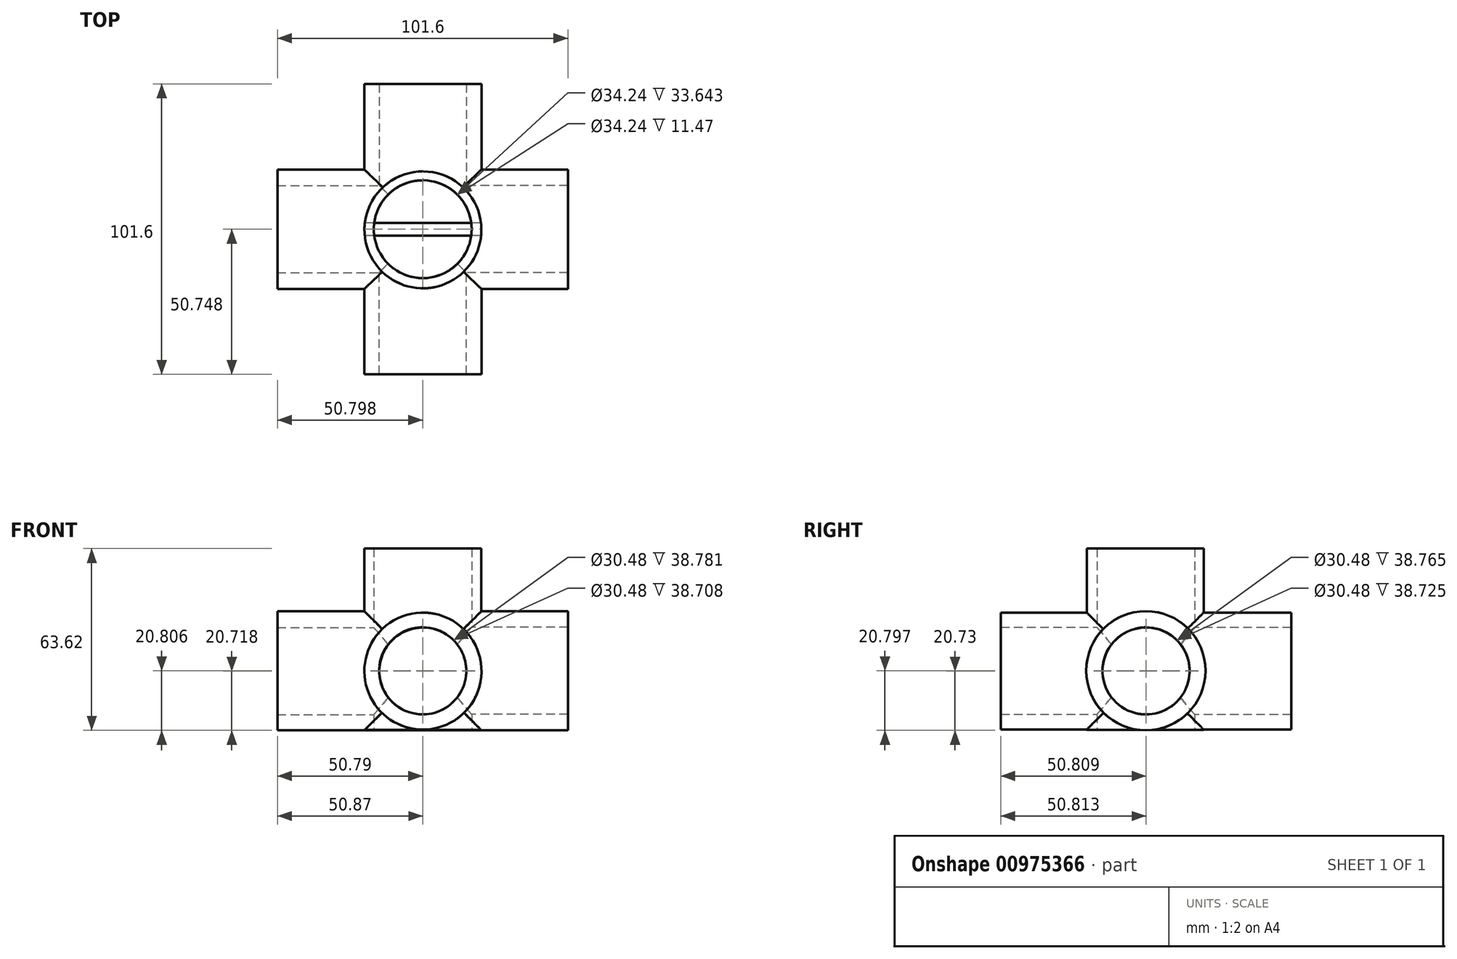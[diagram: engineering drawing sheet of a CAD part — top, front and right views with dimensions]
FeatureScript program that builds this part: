
annotation { "Feature Type Name" : "Feature", "Feature Type Description" : "" }
export const myFeature = defineFeature(function(context is Context, id is Id, definition is map)
    precondition{}
    {
        {
            var Q0;
            Q0=qCreatedBy(makeId("Front.planeOp"),FACE);
            var sketch = newSketch(context, id + "F0", { "sketchPlane" : qUnion([Q0])});
            skCircle(sketch, "E0", {"center": v(0.07, 20.6) * mm, "radius": 20.47 * mm});
            skSolve(sketch);
        }
        {
            var Q0;
            Q0 = qSketchRegion(id + "F0", true);
            extrude(context, id + "F1", {"entities" : qUnion([Q0]), "depth" : 50.8 * mm, "offsetDistance" : 25.4 * mm, "hasSecondDirection" : true, "secondDirectionOppositeDirection" : true, "secondDirectionDepth" : 50.8 * mm});
        }
        {
            var Q0;
            Q0=qCreatedBy(makeId("Top.planeOp"),FACE);
            var sketch = newSketch(context, id + "F2", { "sketchPlane" : qUnion([Q0])});
            skCircle(sketch, "E1", {"center": v(0.07, -0.28) * mm, "radius": 20.46 * mm});
            skSolve(sketch);
        }
        {
            var Q0;
            Q0 = qSketchRegion(id + "F2", true);
            extrude(context, id + "F3", {"entities" : qUnion([Q0]), "operationType" : NewBodyOperationType.ADD, "depth" : 63.5 * mm, "offsetDistance" : 25.4 * mm});
        }
        {
            var Q0;
            Q0=qCreatedBy(makeId("Right.planeOp"),FACE);
            var sketch = newSketch(context, id + "F4", { "sketchPlane" : qUnion([Q0])});
            skCircle(sketch, "E2", {"center": v(-0.07, 20.74) * mm, "radius": 20.86 * mm});
            skSolve(sketch);
        }
        {
            var Q0;
            Q0 = qSketchRegion(id + "F4", true);
            extrude(context, id + "F5", {"entities" : qUnion([Q0]), "operationType" : NewBodyOperationType.ADD, "depth" : 50.8 * mm, "offsetDistance" : 25.4 * mm, "hasSecondDirection" : true, "secondDirectionOppositeDirection" : true, "secondDirectionDepth" : 50.8 * mm});
        }
        {
            var Q0;
            Q0=qCreatedBy(makeId("Right.planeOp"),FACE);
            var sketch = newSketch(context, id + "F6", { "sketchPlane" : qUnion([Q0])});
            skPoint(sketch, "E3", {"position": v(0, 20.61) * mm});
            skSolve(sketch);
        }
        {
            var Q0;
            Q0=sQuery(id+"F6.wireOp",VERTEX,"E3");
            var Q1;
            Q1=makeQuery(id+"F1.opExtrude","SWEPT_BODY",BODY,{"disambiguationData":[OSD([sQuery(id+"F0.wireOp",EDGE,"E0")])]});
            hole(context, id + "F7", {"style" : HoleStyle.SIMPLE, "endStyle" : HoleEndStyle.THROUGH, "holeDiameter" : 30.48 * mm, "majorDiameter" : 6.35 * mm, "isTappedThrough" : true, "tappedDepth" : 12.7 * mm, "tapClearance" : 3, "locations" : qUnion([Q0]), "scope" : qUnion([Q1])});
        }
        {
            var Q0;
            Q0=qCreatedBy(makeId("Right.planeOp"),FACE);
            var sketch = newSketch(context, id + "F8", { "sketchPlane" : qUnion([Q0])});
            skPoint(sketch, "E4", {"position": v(0.01, 20.68) * mm});
            skSolve(sketch);
        }
        {
            var Q0;
            Q0=sQuery(id+"F0.wireOp",VERTEX,"E0.center");
            var Q1;
            Q1=makeQuery(id+"F1.opExtrude","SWEPT_BODY",BODY,{"disambiguationData":[OSD([sQuery(id+"F0.wireOp",EDGE,"E0")])]});
            hole(context, id + "F9", {"style" : HoleStyle.SIMPLE, "endStyle" : HoleEndStyle.THROUGH, "holeDiameter" : 30.48 * mm, "majorDiameter" : 6.35 * mm, "isTappedThrough" : true, "tappedDepth" : 12.7 * mm, "tapClearance" : 3, "locations" : qUnion([Q0]), "scope" : qUnion([Q1])});
        }
        {
            var Q0;
            Q0=sQuery(id+"F8.wireOp",VERTEX,"E4");
            var Q1;
            Q1=makeQuery(id+"F1.opExtrude","SWEPT_BODY",BODY,{"disambiguationData":[OSD([sQuery(id+"F0.wireOp",EDGE,"E0")])]});
            hole(context, id + "F10", {"style" : HoleStyle.SIMPLE, "endStyle" : HoleEndStyle.THROUGH, "oppositeDirection" : true, "holeDiameter" : 30.48 * mm, "majorDiameter" : 6.35 * mm, "isTappedThrough" : true, "tappedDepth" : 12.7 * mm, "tapClearance" : 3, "locations" : qUnion([Q0]), "scope" : qUnion([Q1])});
        }
        {
            var Q0;
            Q0=qCreatedBy(makeId("Front.planeOp"),FACE);
            var sketch = newSketch(context, id + "F11", { "sketchPlane" : qUnion([Q0])});
            skPoint(sketch, "E5", {"position": v(-0.01, 20.69) * mm});
            skSolve(sketch);
        }
        {
            var Q0;
            Q0=sQuery(id+"F11.wireOp",VERTEX,"E5");
            var Q1;
            Q1=makeQuery(id+"F1.opExtrude","SWEPT_BODY",BODY,{"disambiguationData":[OSD([sQuery(id+"F0.wireOp",EDGE,"E0")])]});
            hole(context, id + "F12", {"style" : HoleStyle.SIMPLE, "endStyle" : HoleEndStyle.THROUGH, "oppositeDirection" : true, "holeDiameter" : 30.48 * mm, "majorDiameter" : 6.35 * mm, "isTappedThrough" : true, "tappedDepth" : 12.7 * mm, "tapClearance" : 3, "locations" : qUnion([Q0]), "scope" : qUnion([Q1])});
        }
        {
            var Q0;
            Q0=qCreatedBy(makeId("Top.planeOp"),FACE);
            var sketch = newSketch(context, id + "F13", { "sketchPlane" : qUnion([Q0])});
            skPoint(sketch, "E6", {"position": v(0, -0.05) * mm});
            skCircle(sketch, "E7", {"center": v(0, -0.05) * mm, "radius": 17.12 * mm});
            skSolve(sketch);
        }
        {
            var Q0;
            Q0 = qSketchRegion(id + "F13", true);
            extrude(context, id + "F14", {"entities" : qUnion([Q0]), "operationType" : NewBodyOperationType.REMOVE, "depth" : 84.58 * mm, "offsetDistance" : 25.4 * mm});
        }
    });
